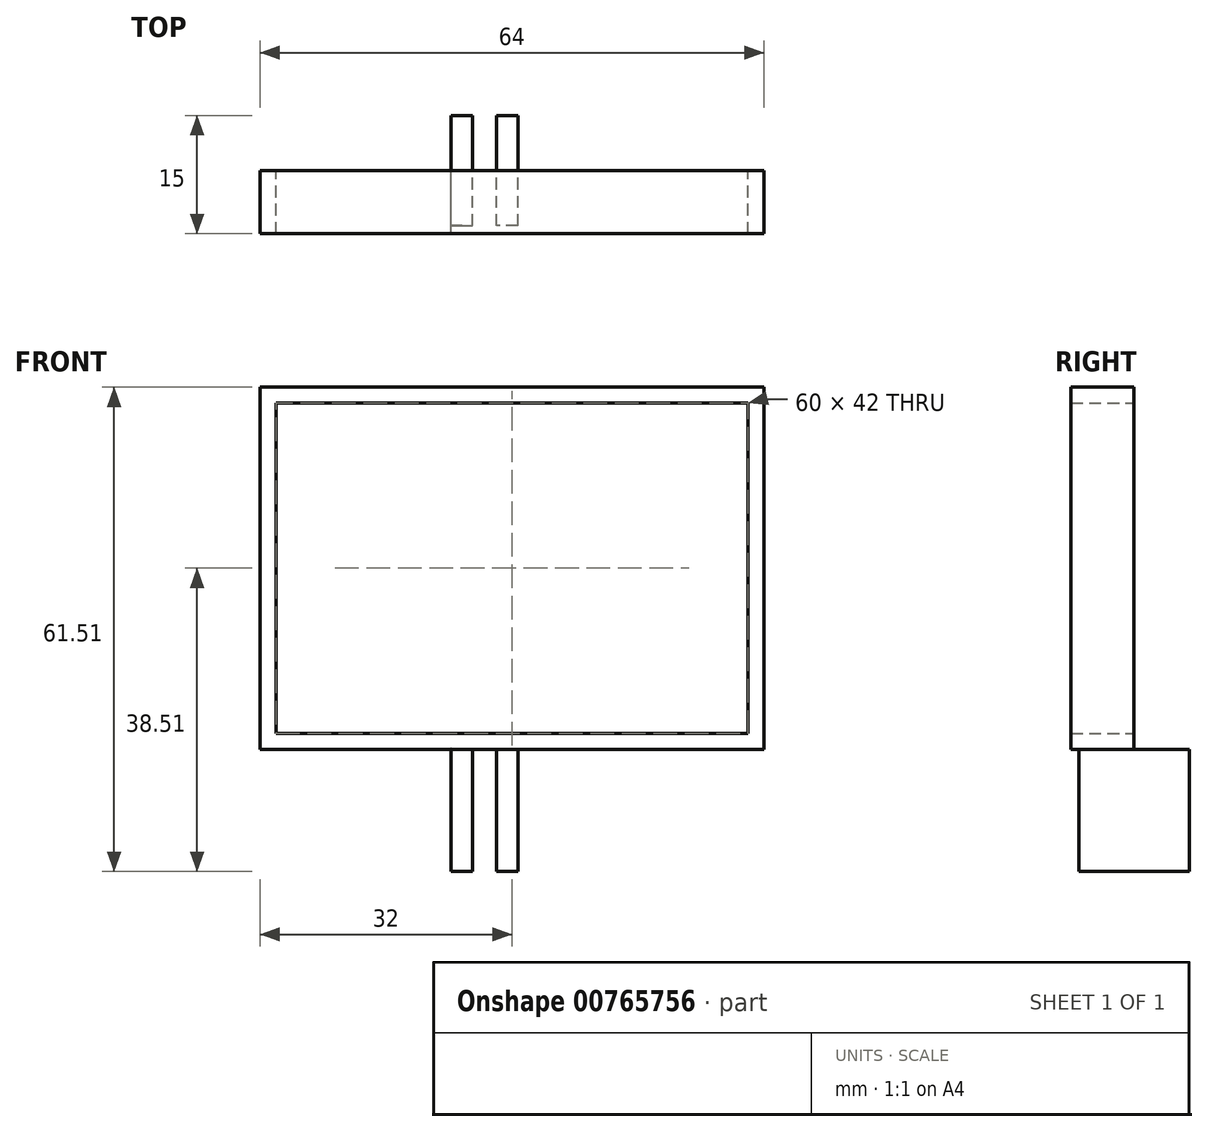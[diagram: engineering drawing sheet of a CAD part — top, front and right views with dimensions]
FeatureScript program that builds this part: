
annotation { "Feature Type Name" : "Feature", "Feature Type Description" : "" }
export const myFeature = defineFeature(function(context is Context, id is Id, definition is map)
    precondition{}
    {
        {
            var Q0;
            Q0=qCreatedBy(makeId("Front.planeOp"),FACE);
            var sketch = newSketch(context, id + "F0", { "sketchPlane" : qUnion([Q0])});
            skLineSegment(sketch, "E0.bottom", {"start": v(30, -21) * mm, "end": v(-30, -21) * mm});
            skLineSegment(sketch, "E0.top", {"start": v(30, 21) * mm, "end": v(-30, 21) * mm});
            skLineSegment(sketch, "E0.left", {"start": v(30, -21) * mm, "end": v(30, 21) * mm});
            skLineSegment(sketch, "E0.right", {"start": v(-30, -21) * mm, "end": v(-30, 21) * mm});
            skPoint(sketch, "E0.middle", {"position": v(0, 0) * mm});
            skLineSegment(sketch, "E1.0", {"start": v(-32, -23) * mm, "end": v(-32, 23) * mm});
            skLineSegment(sketch, "E1.1", {"start": v(32, -23) * mm, "end": v(-32, -23) * mm});
            skLineSegment(sketch, "E1.2", {"start": v(32, -23) * mm, "end": v(32, 23) * mm});
            skLineSegment(sketch, "E1.3", {"start": v(32, 23) * mm, "end": v(-32, 23) * mm});
            skLineSegment(sketch, "E2.bottom", {"start": v(-7.73, -38.49) * mm, "end": v(-5.03, -38.51) * mm});
            skLineSegment(sketch, "E2.left", {"start": v(-7.73, -38.49) * mm, "end": v(-7.73, -22.99) * mm});
            skLineSegment(sketch, "E2.right", {"start": v(-5.03, -38.51) * mm, "end": v(-5.03, -23.01) * mm});
            skPoint(sketch, "E2.middle", {"position": v(-6.38, -23) * mm});
            skLineSegment(sketch, "E3.bottom", {"start": v(0.76, -38.5) * mm, "end": v(-1.94, -38.5) * mm});
            skLineSegment(sketch, "E3.left", {"start": v(0.76, -38.5) * mm, "end": v(0.76, -23) * mm});
            skLineSegment(sketch, "E3.right", {"start": v(-1.94, -38.5) * mm, "end": v(-1.94, -23) * mm});
            skPoint(sketch, "E3.middle", {"position": v(-0.6, -23) * mm});
            skLineSegment(sketch, "E4", {"start": v(-7.73, -22.99) * mm, "end": v(-5.03, -23.01) * mm});
            skLineSegment(sketch, "E5", {"start": v(-5.03, -23.01) * mm, "end": v(0.76, -23) * mm});
            skPoint(sketch, "E6.orphan", {"position": v(-1.94, -7.5) * mm});
            skPoint(sketch, "E7.orphan", {"position": v(0.76, -7.5) * mm});
            skPoint(sketch, "E8.orphan", {"position": v(-5.03, -7.51) * mm});
            skPoint(sketch, "E9.orphan", {"position": v(-7.73, -7.49) * mm});
            skLineSegment(sketch, "E10.bottom", {"start": v(-32, -23) * mm, "end": v(-7.73, -23) * mm});
            skLineSegment(sketch, "E10.left", {"start": v(-32, -23) * mm, "end": v(-32, -7.49) * mm});
            skLineSegment(sketch, "E10.right", {"start": v(-7.73, -23) * mm, "end": v(-7.73, -21) * mm});
            skLineSegment(sketch, "E11.bottom", {"start": v(32, -23) * mm, "end": v(0.76, -23) * mm});
            skLineSegment(sketch, "E11.left", {"start": v(32, -23) * mm, "end": v(32, -7.5) * mm});
            skLineSegment(sketch, "E11.right", {"start": v(0.76, -23) * mm, "end": v(0.76, -21) * mm});
            skSolve(sketch);
        }
        {
            var Q0;
            {var subQ1=sQuery(id+"F0.wireOp",EDGE,"E0.top");Q0=makeQuery(id+"F0.imprint","IMPRINT",FACE,{"disambiguationData":[TD([[makeQuery(id+"F0.imprint","IMPRINT",EDGE,{"derivedFrom":subQ1}),-1.0]])]});}
            var Q1;
            {var subQ4=sQuery(id+"F0.wireOp",EDGE,"E11.bottom");Q1=makeQuery(id+"F0.imprint","IMPRINT",FACE,{"disambiguationData":[TD([[makeQuery(id+"F0.imprint","IMPRINT",EDGE,{"derivedFrom":subQ4}),-1.0]])]});}
            var Q2;
            {var subQ8=sQuery(id+"F0.wireOp",EDGE,"E10.bottom");Q2=makeQuery(id+"F0.imprint","IMPRINT",FACE,{"disambiguationData":[TD([[makeQuery(id+"F0.imprint","IMPRINT",EDGE,{"derivedFrom":subQ8}),1.0]])]});}
            var Q3;
            {var subQ3=sQuery(id+"F0.wireOp",EDGE,"E0.bottom");var subQ7=sQuery(id+"F0.wireOp",EDGE,"E11.right");var subQ9=makeQuery(id+"F0.imprint","INTERSECT",VERTEX,{"derivedFrom":[subQ3,subQ7]});Q3=makeQuery(id+"F0.imprint","IMPRINT",FACE,{"disambiguationData":[TD([[makeQuery(id+"F0.imprint","IMPRINT",EDGE,{"disambiguationData":[TD([[subQ9,-1.0]])],"derivedFrom":subQ3}),1.0]])]});}
            extrude(context, id + "F1", {"entities" : qUnion([Q0, Q1, Q2, Q3]), "depth" : 8 * mm, "offsetDistance" : 25 * mm});
        }
        {
            var Q0;
            Q0=makeQuery(id+"F0.imprint","IMPRINT",FACE,{"disambiguationData":[TD([[makeQuery(id+"F0.imprint","IMPRINT",EDGE,{"derivedFrom":sQuery(id+"F0.wireOp",EDGE,"E2.bottom")}),1.0]])]});
            var Q1;
            Q1=makeQuery(id+"F0.imprint","IMPRINT",FACE,{"disambiguationData":[TD([[makeQuery(id+"F0.imprint","IMPRINT",EDGE,{"derivedFrom":sQuery(id+"F0.wireOp",EDGE,"E3.bottom")}),-1.0]])]});
            extrude(context, id + "F2", {"entities" : qUnion([Q0, Q1]), "depth" : 7 * mm, "offsetDistance" : 25 * mm, "hasSecondDirection" : true, "secondDirectionOppositeDirection" : true, "secondDirectionDepth" : 7 * mm});
        }
    });
